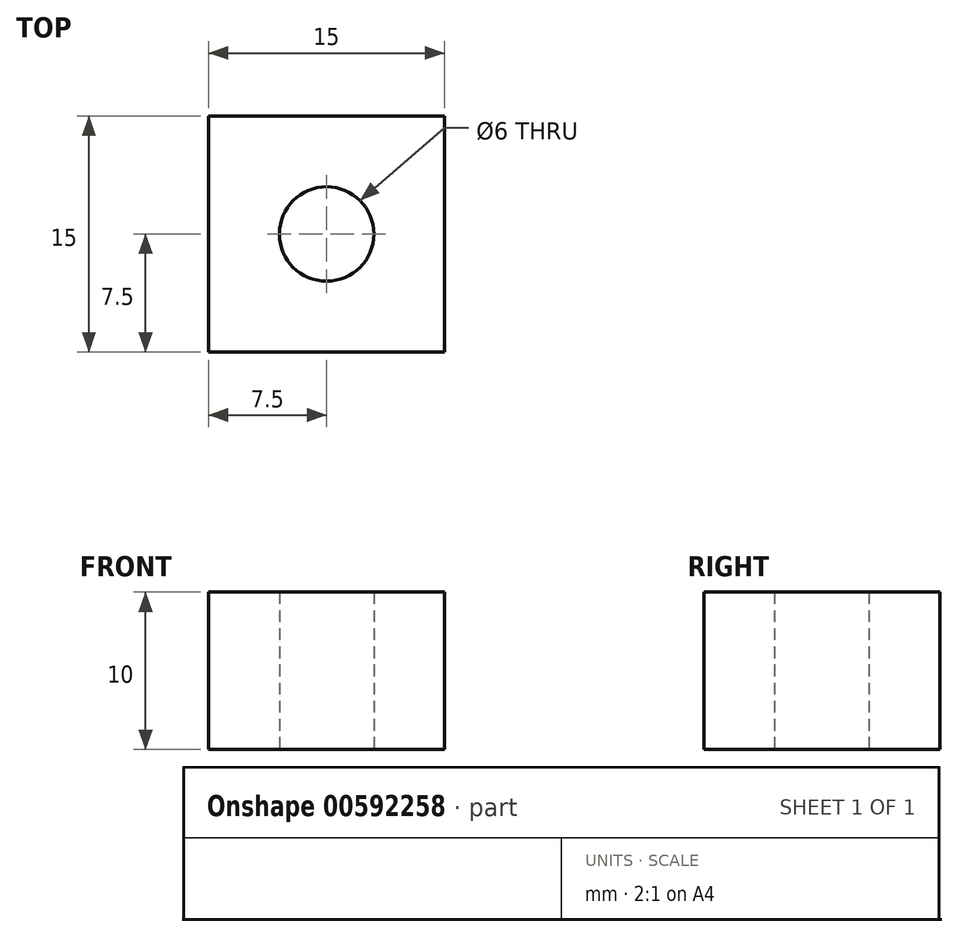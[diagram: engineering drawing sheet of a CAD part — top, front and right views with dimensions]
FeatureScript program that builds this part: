
annotation { "Feature Type Name" : "Feature", "Feature Type Description" : "" }
export const myFeature = defineFeature(function(context is Context, id is Id, definition is map)
    precondition{}
    {
        {
            var Q0;
            Q0=qCreatedBy(makeId("Top.planeOp"),FACE);
            var sketch = newSketch(context, id + "F0", { "sketchPlane" : qUnion([Q0])});
            skLineSegment(sketch, "E0.bottom", {"start": v(7.5, -7.5) * mm, "end": v(-7.5, -7.5) * mm});
            skLineSegment(sketch, "E0.top", {"start": v(7.5, 7.5) * mm, "end": v(-7.5, 7.5) * mm});
            skLineSegment(sketch, "E0.left", {"start": v(7.5, -7.5) * mm, "end": v(7.5, 7.5) * mm});
            skLineSegment(sketch, "E0.right", {"start": v(-7.5, -7.5) * mm, "end": v(-7.5, 7.5) * mm});
            skPoint(sketch, "E0.middle", {"position": v(0, 0) * mm});
            skCircle(sketch, "E1", {"center": v(0, 0) * mm, "radius": 3 * mm});
            skSolve(sketch);
        }
        {
            var Q0;
            Q0=makeQuery(id+"F0.imprint","IMPRINT",FACE,{"disambiguationData":[TD([[makeQuery(id+"F0.imprint","IMPRINT",EDGE,{"derivedFrom":sQuery(id+"F0.wireOp",EDGE,"E0.bottom")}),-1.0]])]});
            extrude(context, id + "F1", {"entities" : qUnion([Q0]), "depth" : 10 * mm, "offsetDistance" : 25 * mm});
        }
    });
